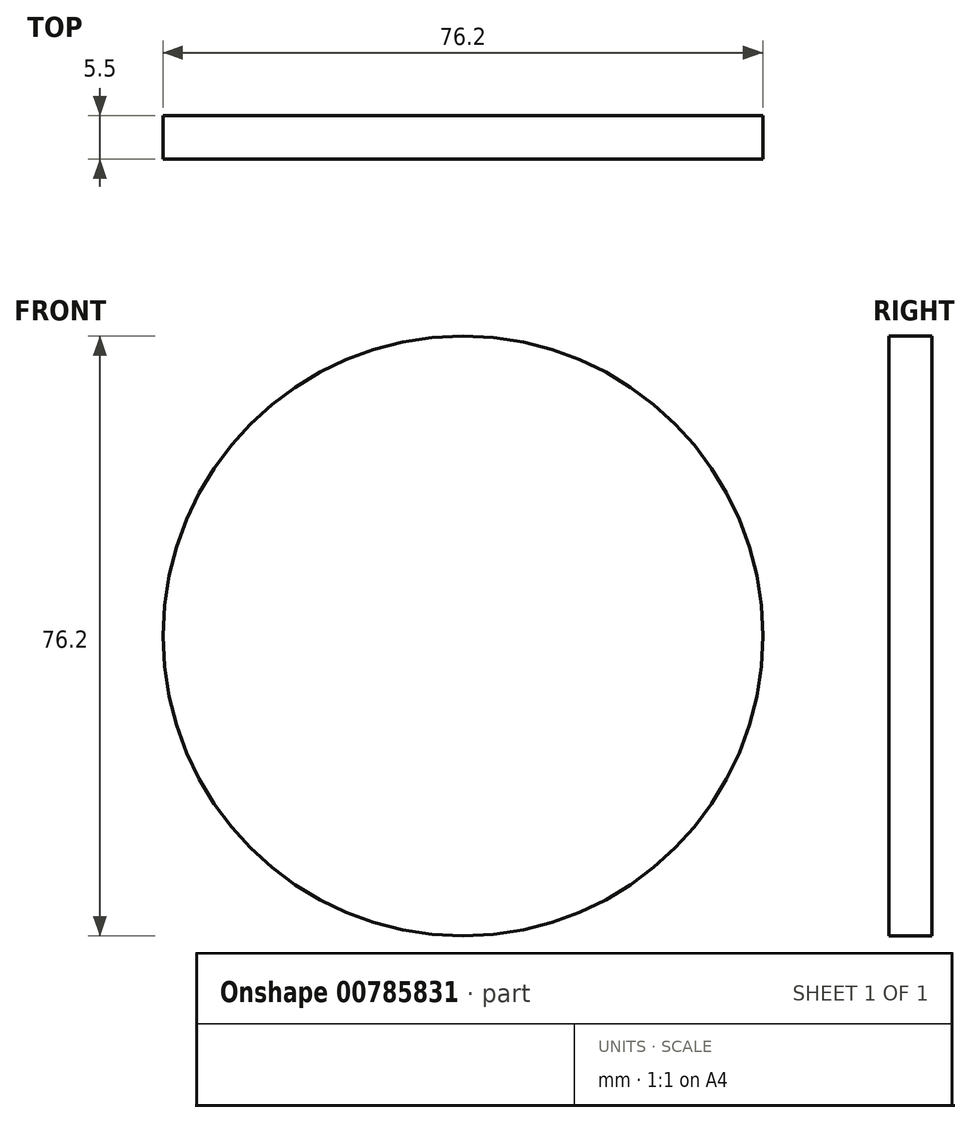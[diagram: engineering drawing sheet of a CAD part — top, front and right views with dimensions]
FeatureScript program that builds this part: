
annotation { "Feature Type Name" : "Feature", "Feature Type Description" : "" }
export const myFeature = defineFeature(function(context is Context, id is Id, definition is map)
    precondition{}
    {
        {
            var Q0;
            Q0=qCreatedBy(makeId("Front.planeOp"),FACE);
            var sketch = newSketch(context, id + "F0", { "sketchPlane" : qUnion([Q0])});
            skCircle(sketch, "E0", {"center": v(-26.63, 8.72) * mm, "radius": 38.1 * mm});
            skSolve(sketch);
        }
        {
            var Q0;
            Q0=makeQuery(id+"F0.imprint","IMPRINT",FACE,{"disambiguationData":[TD([[makeQuery(id+"F0.imprint","IMPRINT",EDGE,{"derivedFrom":sQuery(id+"F0.wireOp",EDGE,"E0")}),1.0]])]});
            extrude(context, id + "F1", {"entities" : qUnion([Q0]), "depth" : 5.5 * mm, "offsetDistance" : 25.4 * mm});
        }
    });
